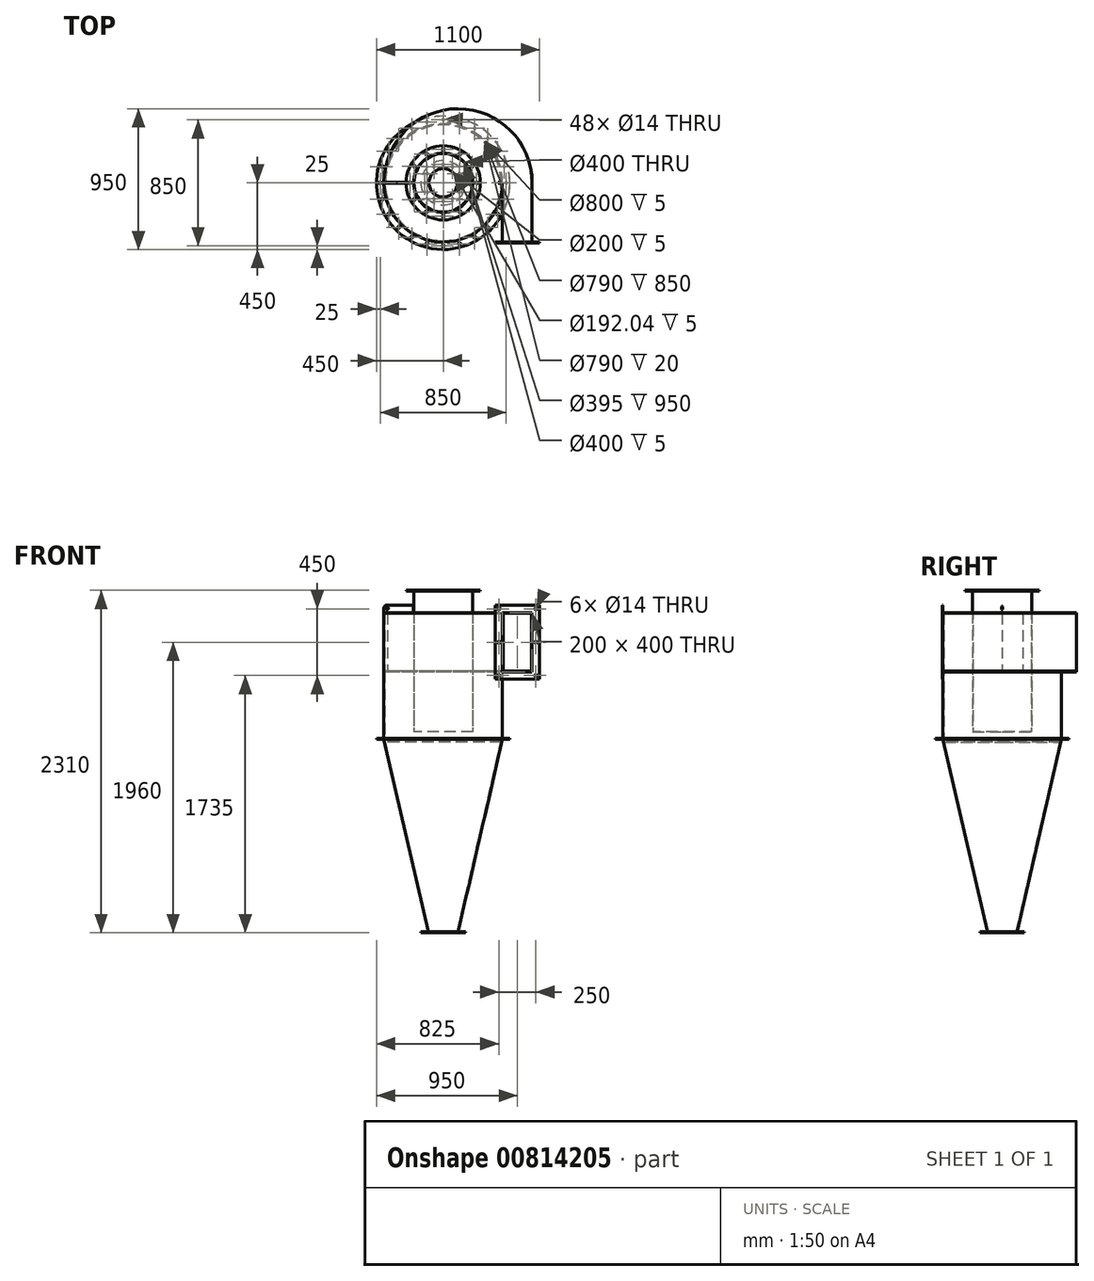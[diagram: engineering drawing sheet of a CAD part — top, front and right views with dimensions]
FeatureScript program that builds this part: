
annotation { "Feature Type Name" : "Feature", "Feature Type Description" : "" }
export const myFeature = defineFeature(function(context is Context, id is Id, definition is map)
    precondition{}
    {
        {
            var Q0;
            Q0=qCreatedBy(makeId("Top.planeOp"),FACE);
            var sketch = newSketch(context, id + "F0", { "sketchPlane" : qUnion([Q0])});
            skCircle(sketch, "E0", {"center": v(0, 0) * mm, "radius": 150 * mm});
            skCircle(sketch, "E1", {"center": v(0, 0) * mm, "radius": 100 * mm});
            skLineSegment(sketch, "E2", {"start": v(0, 100) * mm, "end": v(0, 150) * mm, "construction": true});
            skCircle(sketch, "E3", {"center": v(0, 125) * mm, "radius": 7 * mm});
            skCircle(sketch, "E4.1.0", {"center": v(-62.5, 108.25) * mm, "radius": 7 * mm});
            skCircle(sketch, "E4.2.0", {"center": v(-108.25, 62.5) * mm, "radius": 7 * mm});
            skCircle(sketch, "E4.3.0", {"center": v(-125, 0) * mm, "radius": 7 * mm});
            skCircle(sketch, "E4.4.0", {"center": v(-108.25, -62.5) * mm, "radius": 7 * mm});
            skCircle(sketch, "E4.5.0", {"center": v(-62.5, -108.25) * mm, "radius": 7 * mm});
            skCircle(sketch, "E4.6.0", {"center": v(0, -125) * mm, "radius": 7 * mm});
            skCircle(sketch, "E4.7.0", {"center": v(62.5, -108.25) * mm, "radius": 7 * mm});
            skCircle(sketch, "E4.8.0", {"center": v(108.25, -62.5) * mm, "radius": 7 * mm});
            skCircle(sketch, "E4.9.0", {"center": v(125, 0) * mm, "radius": 7 * mm});
            skCircle(sketch, "E4.10.0", {"center": v(108.25, 62.5) * mm, "radius": 7 * mm});
            skCircle(sketch, "E4.11.0", {"center": v(62.5, 108.25) * mm, "radius": 7 * mm});
            skSolve(sketch);
        }
        {
            var Q0;
            Q0=makeQuery(id+"F0.imprint","IMPRINT",FACE,{"disambiguationData":[TD([[makeQuery(id+"F0.imprint","IMPRINT",EDGE,{"derivedFrom":sQuery(id+"F0.wireOp",EDGE,"E0")}),1.0]])]});
            extrude(context, id + "F1", {"entities" : qUnion([Q0]), "oppositeDirection" : true, "depth" : 5 * mm, "offsetDistance" : 25 * mm});
        }
        {
            var Q0;
            Q0=makeQuery(id+"F0.imprint","IMPRINT",FACE,{"disambiguationData":[TD([[makeQuery(id+"F0.imprint","IMPRINT",EDGE,{"derivedFrom":sQuery(id+"F0.wireOp",EDGE,"E0")}),1.0]])]});
            cPlane(context, id + "F2", {"entities" : qUnion([Q0]), "cplaneType" : CPlaneType.OFFSET, "offset" : 1300 * mm, "width" : 150 * mm, "height" : 150 * mm});
        }
        {
            var Q0;
            Q0=qCreatedBy(id+"F2.planeOp",FACE);
            var sketch = newSketch(context, id + "F3", { "sketchPlane" : qUnion([Q0])});
            skCircle(sketch, "E5", {"center": v(0, 0) * mm, "radius": 400 * mm});
            skCircle(sketch, "E6", {"center": v(0, 0) * mm, "radius": 450 * mm});
            skLineSegment(sketch, "E7", {"start": v(0, 400) * mm, "end": v(0, 450) * mm, "construction": true});
            skCircle(sketch, "E8", {"center": v(0, 425) * mm, "radius": 7 * mm});
            skCircle(sketch, "E9.1.0", {"center": v(-110, 410.52) * mm, "radius": 7 * mm});
            skCircle(sketch, "E9.2.0", {"center": v(-212.5, 368.06) * mm, "radius": 7 * mm});
            skCircle(sketch, "E9.3.0", {"center": v(-300.52, 300.52) * mm, "radius": 7 * mm});
            skCircle(sketch, "E9.4.0", {"center": v(-368.06, 212.5) * mm, "radius": 7 * mm});
            skCircle(sketch, "E9.5.0", {"center": v(-410.52, 110) * mm, "radius": 7 * mm});
            skCircle(sketch, "E9.6.0", {"center": v(-425, 0) * mm, "radius": 7 * mm});
            skCircle(sketch, "E9.7.0", {"center": v(-410.52, -110) * mm, "radius": 7 * mm});
            skCircle(sketch, "E9.8.0", {"center": v(-368.06, -212.5) * mm, "radius": 7 * mm});
            skCircle(sketch, "E9.9.0", {"center": v(-300.52, -300.52) * mm, "radius": 7 * mm});
            skCircle(sketch, "E9.10.0", {"center": v(-212.5, -368.06) * mm, "radius": 7 * mm});
            skCircle(sketch, "E9.11.0", {"center": v(-110, -410.52) * mm, "radius": 7 * mm});
            skCircle(sketch, "E9.12.0", {"center": v(0, -425) * mm, "radius": 7 * mm});
            skCircle(sketch, "E9.13.0", {"center": v(110, -410.52) * mm, "radius": 7 * mm});
            skCircle(sketch, "E9.14.0", {"center": v(212.5, -368.06) * mm, "radius": 7 * mm});
            skCircle(sketch, "E9.15.0", {"center": v(300.52, -300.52) * mm, "radius": 7 * mm});
            skCircle(sketch, "E9.16.0", {"center": v(368.06, -212.5) * mm, "radius": 7 * mm});
            skCircle(sketch, "E9.17.0", {"center": v(410.52, -110) * mm, "radius": 7 * mm});
            skCircle(sketch, "E9.18.0", {"center": v(425, 0) * mm, "radius": 7 * mm});
            skCircle(sketch, "E9.19.0", {"center": v(410.52, 110) * mm, "radius": 7 * mm});
            skCircle(sketch, "E9.20.0", {"center": v(368.06, 212.5) * mm, "radius": 7 * mm});
            skCircle(sketch, "E9.21.0", {"center": v(300.52, 300.52) * mm, "radius": 7 * mm});
            skCircle(sketch, "E9.22.0", {"center": v(212.5, 368.06) * mm, "radius": 7 * mm});
            skCircle(sketch, "E9.23.0", {"center": v(110, 410.52) * mm, "radius": 7 * mm});
            skSolve(sketch);
        }
        {
            var Q0;
            Q0=makeQuery(id+"F3.imprint","IMPRINT",FACE,{"disambiguationData":[TD([[makeQuery(id+"F3.imprint","IMPRINT",EDGE,{"derivedFrom":sQuery(id+"F3.wireOp",EDGE,"E5")}),-1.0]])]});
            extrude(context, id + "F4", {"entities" : qUnion([Q0]), "depth" : 5 * mm, "offsetDistance" : 25 * mm});
        }
        {
            var Q0;
            Q0=qCreatedBy(makeId("Top.planeOp"),FACE);
            var sketch = newSketch(context, id + "F5", { "sketchPlane" : qUnion([Q0])});
            skCircle(sketch, "E10", {"center": v(0, 0) * mm, "radius": 100 * mm});
            skSolve(sketch);
        }
        {
            var Q0;
            Q0=qCreatedBy(id+"F2.planeOp",FACE);
            var sketch = newSketch(context, id + "F6", { "sketchPlane" : qUnion([Q0])});
            skCircle(sketch, "E11", {"center": v(0, 0) * mm, "radius": 400 * mm});
            skLineSegment(sketch, "E12", {"start": v(0, 0) * mm, "end": v(0, 559.62) * mm, "construction": true});
            skSolve(sketch);
        }
        {
            var Q0;
            Q0=makeQuery(id+"F5.imprint","IMPRINT",FACE,{"disambiguationData":[TD([[makeQuery(id+"F5.imprint","IMPRINT",EDGE,{"derivedFrom":sQuery(id+"F5.wireOp",EDGE,"E10")}),1.0]])]});
            var Q1;
            Q1=makeQuery(id+"F6.imprint","IMPRINT",FACE,{"disambiguationData":[TD([[makeQuery(id+"F6.imprint","IMPRINT",EDGE,{"derivedFrom":sQuery(id+"F6.wireOp",EDGE,"E11")}),1.0]])]});
            loft(context, id + "F7", {"sheetProfilesArray" : [{ "sheetProfileEntities" : qUnion([Q0]) }, { "sheetProfileEntities" : qUnion([Q1]) }]});
        }
        {
            var Q0;
            Q0=makeQuery(id+"F7.opLoft","CAP_FACE",FACE,{"disambiguationData":[OSD([makeQuery(id+"F6.imprint","IMPRINT",FACE,{"disambiguationData":[TD([[makeQuery(id+"F6.imprint","IMPRINT",EDGE,{"derivedFrom":sQuery(id+"F6.wireOp",EDGE,"E11")}),1.0]])]})])],"isStart":true});
            shell(context, id + "F8", {"entities" : qUnion([Q0]), "thickness" : 5 * mm});
        }
        {
            var Q0;
            Q0=makeQuery(id+"F8.opShell","OFFSET_FACE",FACE,{"disambiguationData":[OSD([makeQuery(id+"F5.imprint","IMPRINT",FACE,{"disambiguationData":[TD([[makeQuery(id+"F5.imprint","IMPRINT",EDGE,{"derivedFrom":sQuery(id+"F5.wireOp",EDGE,"E10")}),1.0]])]})])]});
            extrude(context, id + "F9", {"entities" : qUnion([Q0]), "operationType" : NewBodyOperationType.REMOVE, "oppositeDirection" : true, "depth" : 25 * mm, "offsetDistance" : 25 * mm});
        }
        {
            var Q0;
            Q0=qSketchRegion(id+"F6",true);
            extrude(context, id + "F10", {"entities" : qUnion([Q0]), "depth" : 850 * mm, "offsetDistance" : 25 * mm});
        }
        {
            var Q0;
            Q0=makeQuery(id+"F10.opExtrude","CAP_FACE",FACE,{"disambiguationData":[OSD([sQuery(id+"F6.wireOp",EDGE,"E11")])],"isStart":false});
            shell(context, id + "F11", {"entities" : qUnion([Q0]), "thickness" : 5 * mm});
        }
        {
            var Q0;
            {var subQ0=sQuery(id+"F6.wireOp",EDGE,"E11");Q0=makeQuery(id+"F11.opShell","OFFSET_FACE",FACE,{"disambiguationData":[OSD([subQ0]),TDD([makeQuery(id+"F10.opExtrude","CAP_FACE",FACE,{"disambiguationData":[OSD([subQ0])],"isStart":true})])]});}
            extrude(context, id + "F12", {"entities" : qUnion([Q0]), "operationType" : NewBodyOperationType.REMOVE, "oppositeDirection" : true, "depth" : 25 * mm, "offsetDistance" : 25 * mm});
        }
        {
            var Q0;
            Q0=makeQuery(id+"F4.opExtrude","CAP_FACE",FACE,{"disambiguationData":[OSD([sQuery(id+"F3.wireOp",EDGE,"E5"),sQuery(id+"F3.wireOp",EDGE,"E6"),sQuery(id+"F3.wireOp",EDGE,"E8"),sQuery(id+"F3.wireOp",EDGE,"E9.1.0"),sQuery(id+"F3.wireOp",EDGE,"E9.2.0"),sQuery(id+"F3.wireOp",EDGE,"E9.3.0"),sQuery(id+"F3.wireOp",EDGE,"E9.4.0"),sQuery(id+"F3.wireOp",EDGE,"E9.5.0"),sQuery(id+"F3.wireOp",EDGE,"E9.6.0"),sQuery(id+"F3.wireOp",EDGE,"E9.7.0"),sQuery(id+"F3.wireOp",EDGE,"E9.8.0"),sQuery(id+"F3.wireOp",EDGE,"E9.9.0"),sQuery(id+"F3.wireOp",EDGE,"E9.10.0"),sQuery(id+"F3.wireOp",EDGE,"E9.11.0"),sQuery(id+"F3.wireOp",EDGE,"E9.12.0"),sQuery(id+"F3.wireOp",EDGE,"E9.13.0"),sQuery(id+"F3.wireOp",EDGE,"E9.14.0"),sQuery(id+"F3.wireOp",EDGE,"E9.15.0"),sQuery(id+"F3.wireOp",EDGE,"E9.16.0"),sQuery(id+"F3.wireOp",EDGE,"E9.17.0"),sQuery(id+"F3.wireOp",EDGE,"E9.18.0"),sQuery(id+"F3.wireOp",EDGE,"E9.19.0"),sQuery(id+"F3.wireOp",EDGE,"E9.20.0"),sQuery(id+"F3.wireOp",EDGE,"E9.21.0"),sQuery(id+"F3.wireOp",EDGE,"E9.22.0"),sQuery(id+"F3.wireOp",EDGE,"E9.23.0")])],"isStart":false});
            cPlane(context, id + "F13", {"entities" : qUnion([Q0]), "cplaneType" : CPlaneType.OFFSET, "offset" : 450 * mm, "width" : 150 * mm, "height" : 150 * mm});
        }
        {
            var Q0;
            Q0=qCreatedBy(id+"F13.planeOp",FACE);
            var sketch = newSketch(context, id + "F14", { "sketchPlane" : qUnion([Q0])});
            skLineSegment(sketch, "E13.bottom", {"start": v(-526.39, 0) * mm, "end": v(526.39, 0) * mm});
            skLineSegment(sketch, "E13.top", {"start": v(-526.39, 503.66) * mm, "end": v(526.39, 503.66) * mm});
            skLineSegment(sketch, "E13.left", {"start": v(-526.39, 0) * mm, "end": v(-526.39, 503.66) * mm});
            skLineSegment(sketch, "E13.right", {"start": v(526.39, 0) * mm, "end": v(526.39, 503.66) * mm});
            skSolve(sketch);
        }
        {
            var Q0;
            Q0=makeQuery(id+"F14.imprint","IMPRINT",FACE,{"disambiguationData":[TD([[makeQuery(id+"F14.imprint","IMPRINT",EDGE,{"derivedFrom":sQuery(id+"F14.wireOp",EDGE,"E13.bottom")}),1.0]])]});
            extrude(context, id + "F15", {"entities" : qUnion([Q0]), "operationType" : NewBodyOperationType.REMOVE, "depth" : 400 * mm, "offsetDistance" : 25 * mm});
        }
        {
            var Q0;
            Q0=qCreatedBy(id+"F13.planeOp",FACE);
            var sketch = newSketch(context, id + "F16", { "sketchPlane" : qUnion([Q0])});
            skArc(sketch, "E14", {"start": v(600, 0) * mm, "mid": v(100, 500) * mm, "end": v(-400, 0) * mm});
            skLineSegment(sketch, "E15", {"start": v(-400, 0) * mm, "end": v(721.85, 0) * mm, "construction": true});
            skLineSegment(sketch, "E16", {"start": v(600, 0) * mm, "end": v(600, -400) * mm});
            skLineSegment(sketch, "E17", {"start": v(600, -400) * mm, "end": v(400, -400) * mm});
            skLineSegment(sketch, "E18", {"start": v(400, -400) * mm, "end": v(400, 0) * mm});
            skArc(sketch, "E19", {"start": v(400, 0) * mm, "mid": v(0, 400) * mm, "end": v(-400, 0) * mm});
            skSolve(sketch);
        }
        {
            var Q0;
            Q0=makeQuery(id+"F16.imprint","IMPRINT",FACE,{"disambiguationData":[TD([[makeQuery(id+"F16.imprint","IMPRINT",EDGE,{"derivedFrom":sQuery(id+"F16.wireOp",EDGE,"E14")}),1.0]])]});
            extrude(context, id + "F17", {"entities" : qUnion([Q0]), "depth" : 5 * mm, "offsetDistance" : 25 * mm});
        }
        {
            var Q0;
            Q0=makeQuery(id+"F17.opExtrude","CAP_FACE",FACE,{"disambiguationData":[OSD([sQuery(id+"F16.wireOp",EDGE,"E14"),sQuery(id+"F16.wireOp",EDGE,"E16"),sQuery(id+"F16.wireOp",EDGE,"E17"),sQuery(id+"F16.wireOp",EDGE,"E18"),sQuery(id+"F16.wireOp",EDGE,"E19")])],"isStart":false});
            var sketch = newSketch(context, id + "F18", { "sketchPlane" : qUnion([Q0])});
            skLineSegment(sketch, "E20.bottom", {"start": v(400, -400) * mm, "end": v(405, -400) * mm});
            skLineSegment(sketch, "E20.top", {"start": v(400, 0) * mm, "end": v(405, 0) * mm});
            skLineSegment(sketch, "E20.left", {"start": v(400, -400) * mm, "end": v(400, 0) * mm});
            skLineSegment(sketch, "E20.right", {"start": v(405, -400) * mm, "end": v(405, 0) * mm});
            skSolve(sketch);
        }
        {
            var Q0;
            Q0=makeQuery(id+"F18.imprint","IMPRINT",FACE,{"disambiguationData":[TD([[makeQuery(id+"F18.imprint","IMPRINT",EDGE,{"derivedFrom":sQuery(id+"F18.wireOp",EDGE,"E20.bottom")}),-1.0]])]});
            extrude(context, id + "F19", {"entities" : qUnion([Q0]), "operationType" : NewBodyOperationType.ADD, "depth" : 390 * mm, "offsetDistance" : 25 * mm});
        }
        {
            var Q0;
            Q0=qCreatedBy(id+"F13.planeOp",FACE);
            cPlane(context, id + "F20", {"entities" : qUnion([Q0]), "cplaneType" : CPlaneType.OFFSET, "offset" : 395 * mm, "width" : 150 * mm, "height" : 150 * mm});
        }
        {
            var Q0;
            Q0=qCreatedBy(id+"F20.planeOp",FACE);
            var sketch = newSketch(context, id + "F21", { "sketchPlane" : qUnion([Q0])});
            skArc(sketch, "E21", {"start": v(600, 0) * mm, "mid": v(100, 500) * mm, "end": v(-400, 0) * mm});
            skLineSegment(sketch, "E22", {"start": v(-400, 0) * mm, "end": v(721.85, 0) * mm, "construction": true});
            skLineSegment(sketch, "E23", {"start": v(600, 0) * mm, "end": v(600, -400) * mm});
            skLineSegment(sketch, "E24", {"start": v(600, -400) * mm, "end": v(400, -400) * mm});
            skLineSegment(sketch, "E25", {"start": v(400, -400) * mm, "end": v(400, 0) * mm});
            skArc(sketch, "E26", {"start": v(-400, 0) * mm, "mid": v(0, -400) * mm, "end": v(400, 0) * mm});
            skCircle(sketch, "E27", {"center": v(0, 0) * mm, "radius": 200 * mm});
            skSolve(sketch);
        }
        {
            var Q0;
            Q0=makeQuery(id+"F21.imprint","IMPRINT",FACE,{"disambiguationData":[TD([[makeQuery(id+"F21.imprint","IMPRINT",EDGE,{"derivedFrom":sQuery(id+"F21.wireOp",EDGE,"E21")}),1.0]])]});
            extrude(context, id + "F22", {"entities" : qUnion([Q0]), "depth" : 5 * mm, "offsetDistance" : 25 * mm});
        }
        {
            var Q0;
            Q0=qCreatedBy(id+"F20.planeOp",FACE);
            var sketch = newSketch(context, id + "F23", { "sketchPlane" : qUnion([Q0])});
            skCircle(sketch, "E28", {"center": v(0, 0) * mm, "radius": 199.5 * mm});
            skCircle(sketch, "E29.0", {"center": v(0, 0) * mm, "radius": 197.5 * mm});
            skSolve(sketch);
        }
        {
            var Q0;
            Q0=makeQuery(id+"F23.imprint","IMPRINT",FACE,{"disambiguationData":[TD([[makeQuery(id+"F23.imprint","IMPRINT",EDGE,{"derivedFrom":sQuery(id+"F23.wireOp",EDGE,"E28")}),1.0]])]});
            extrude(context, id + "F24", {"entities" : qUnion([Q0]), "depth" : 950 * mm, "offsetDistance" : 25 * mm});
        }
        {
            var Q0;
            Q0=qCreatedBy(makeId("Front.planeOp"),FACE);
            var sketch = newSketch(context, id + "F25", { "sketchPlane" : qUnion([Q0])});
            skLineSegment(sketch, "E30", {"start": v(0, 0) * mm, "end": v(0, 3754) * mm, "construction": true});
            skSolve(sketch);
        }
        {
            var Q0;
            Q0=makeQuery(id+"F24.opExtrude","SWEPT_BODY",BODY,{"disambiguationData":[OSD([sQuery(id+"F23.wireOp",EDGE,"E28"),sQuery(id+"F23.wireOp",EDGE,"E29.0")])]});
            var Q1;
            Q1=sQuery(id+"F25.wireOp",EDGE,"E30");
            var Q2;
            Q2=sQuery(id+"F25.wireOp",EDGE,"E30");
            transform(context, id + "F26", {"entities" : qUnion([Q0]), "transformType" : TransformType.TRANSLATION_DISTANCE, "transformDirection" : qUnion([Q2]), "distance" : 800 * mm, "oppositeDirection" : true, "makeCopy" : false});
        }
        {
            var Q0;
            Q0=makeQuery(id+"F22.opExtrude","SWEPT_FACE",FACE,{"disambiguationData":[OSD([sQuery(id+"F21.wireOp",EDGE,"E24")])]});
            var sketch = newSketch(context, id + "F27", { "sketchPlane" : qUnion([Q0])});
            skLineSegment(sketch, "E31.bottom", {"start": v(400, 2155) * mm, "end": v(600, 2155) * mm});
            skLineSegment(sketch, "E31.top", {"start": v(400, 1755) * mm, "end": v(600, 1755) * mm});
            skLineSegment(sketch, "E31.left", {"start": v(400, 2155) * mm, "end": v(400, 1755) * mm});
            skLineSegment(sketch, "E31.right", {"start": v(600, 2155) * mm, "end": v(600, 1755) * mm});
            skLineSegment(sketch, "E32.0", {"start": v(650, 2205) * mm, "end": v(650, 1705) * mm});
            skLineSegment(sketch, "E32.1", {"start": v(350, 2205) * mm, "end": v(650, 2205) * mm});
            skLineSegment(sketch, "E32.2", {"start": v(350, 2205) * mm, "end": v(350, 1705) * mm});
            skLineSegment(sketch, "E32.3", {"start": v(350, 1705) * mm, "end": v(650, 1705) * mm});
            skLineSegment(sketch, "E33.0", {"start": v(375, 2180) * mm, "end": v(375, 1730) * mm, "construction": true});
            skLineSegment(sketch, "E33.1", {"start": v(375, 2180) * mm, "end": v(625, 2180) * mm, "construction": true});
            skLineSegment(sketch, "E33.2", {"start": v(625, 2180) * mm, "end": v(625, 1730) * mm, "construction": true});
            skLineSegment(sketch, "E33.3", {"start": v(375, 1730) * mm, "end": v(625, 1730) * mm});
            skCircle(sketch, "E34", {"center": v(375, 2180) * mm, "radius": 7 * mm});
            skCircle(sketch, "E35", {"center": v(625, 2180) * mm, "radius": 7 * mm});
            skCircle(sketch, "E36", {"center": v(625, 1730) * mm, "radius": 7 * mm});
            skCircle(sketch, "E37", {"center": v(375, 1730) * mm, "radius": 7 * mm});
            skCircle(sketch, "E38", {"center": v(375, 1955) * mm, "radius": 7 * mm});
            skCircle(sketch, "E39", {"center": v(625, 1955) * mm, "radius": 7 * mm});
            skSolve(sketch);
        }
        {
            var Q0;
            {var subQ3=sQuery(id+"F27.wireOp",EDGE,"E31.bottom");Q0=makeQuery(id+"F27.imprint","IMPRINT",FACE,{"disambiguationData":[TD([[makeQuery(id+"F27.imprint","IMPRINT",EDGE,{"derivedFrom":subQ3}),-1.0]])]});}
            extrude(context, id + "F28", {"entities" : qUnion([Q0]), "depth" : 5 * mm, "offsetDistance" : 25 * mm});
        }
        {
            var Q0;
            Q0=qCreatedBy(makeId("Front.planeOp"),FACE);
            var sketch = newSketch(context, id + "F29", { "sketchPlane" : qUnion([Q0])});
            skLineSegment(sketch, "E40.bottom", {"start": v(-200.23, 2155) * mm, "end": v(-400.23, 2155) * mm});
            skLineSegment(sketch, "E40.top", {"start": v(-200.23, 2205) * mm, "end": v(-380.23, 2205) * mm});
            skLineSegment(sketch, "E40.left", {"start": v(-200.23, 2155) * mm, "end": v(-200.23, 2205) * mm});
            skLineSegment(sketch, "E40.right", {"start": v(-400.23, 2155) * mm, "end": v(-400.23, 2185) * mm});
            skPoint(sketch, "E41.visualSharp", {"position": v(-400.23, 2205) * mm});
            skArc(sketch, "E41.filletArc", {"start": v(-380.23, 2205) * mm, "mid": v(-394.37, 2199.14) * mm, "end": v(-400.23, 2185) * mm});
            skCircle(sketch, "E42", {"center": v(-380.23, 2185) * mm, "radius": 10 * mm});
            skCircle(sketch, "E43.MirrorC", {"center": v(380.23, 2185) * mm, "radius": 10 * mm});
            skArc(sketch, "E44.MirrorCS", {"start": v(380.23, 2205) * mm, "mid": v(394.37, 2199.14) * mm, "end": v(400.23, 2185) * mm});
            skPoint(sketch, "E45.MirrorP", {"position": v(400.23, 2205) * mm});
            skLineSegment(sketch, "E46.MirrorCS", {"start": v(400.23, 2155) * mm, "end": v(400.23, 2185) * mm});
            skLineSegment(sketch, "E47.MirrorCS", {"start": v(200.23, 2155) * mm, "end": v(200.23, 2205) * mm});
            skLineSegment(sketch, "E48.MirrorCS", {"start": v(200.23, 2155) * mm, "end": v(400.23, 2155) * mm});
            skLineSegment(sketch, "E49.MirrorCS", {"start": v(200.23, 2205) * mm, "end": v(380.23, 2205) * mm});
            skSolve(sketch);
        }
        {
            var Q0;
            Q0=makeQuery(id+"F29.imprint","IMPRINT",FACE,{"disambiguationData":[TD([[makeQuery(id+"F29.imprint","IMPRINT",EDGE,{"derivedFrom":sQuery(id+"F29.wireOp",EDGE,"E40.bottom")}),-1.0]])]});
            var Q1;
            Q1=makeQuery(id+"F29.imprint","IMPRINT",FACE,{"disambiguationData":[TD([[makeQuery(id+"F29.imprint","IMPRINT",EDGE,{"derivedFrom":sQuery(id+"F29.wireOp",EDGE,"E43.MirrorC")}),1.0]])]});
            extrude(context, id + "F30", {"entities" : qUnion([Q0, Q1]), "operationType" : NewBodyOperationType.ADD, "endBound" : BoundingType.SYMMETRIC, "depth" : 5 * mm, "offsetDistance" : 25 * mm});
        }
        {
            var Q0;
            Q0=makeQuery(id+"F24.opExtrude","CAP_FACE",FACE,{"disambiguationData":[OSD([sQuery(id+"F23.wireOp",EDGE,"E28"),sQuery(id+"F23.wireOp",EDGE,"E29.0")])],"isStart":false});
            var sketch = newSketch(context, id + "F31", { "sketchPlane" : qUnion([Q0])});
            skCircle(sketch, "E50", {"center": v(0, 0) * mm, "radius": 200 * mm});
            skCircle(sketch, "E51.0", {"center": v(0, 0) * mm, "radius": 250 * mm});
            skLineSegment(sketch, "E52", {"start": v(0, 200) * mm, "end": v(0, 250) * mm, "construction": true});
            skCircle(sketch, "E53", {"center": v(0, 225) * mm, "radius": 7 * mm});
            skCircle(sketch, "E54.1.0", {"center": v(-112.5, 194.86) * mm, "radius": 7 * mm});
            skCircle(sketch, "E54.2.0", {"center": v(-194.86, 112.5) * mm, "radius": 7 * mm});
            skCircle(sketch, "E54.3.0", {"center": v(-225, 0) * mm, "radius": 7 * mm});
            skCircle(sketch, "E54.4.0", {"center": v(-194.86, -112.5) * mm, "radius": 7 * mm});
            skCircle(sketch, "E54.5.0", {"center": v(-112.5, -194.86) * mm, "radius": 7 * mm});
            skCircle(sketch, "E54.6.0", {"center": v(0, -225) * mm, "radius": 7 * mm});
            skCircle(sketch, "E54.7.0", {"center": v(112.5, -194.86) * mm, "radius": 7 * mm});
            skCircle(sketch, "E54.8.0", {"center": v(194.86, -112.5) * mm, "radius": 7 * mm});
            skCircle(sketch, "E54.9.0", {"center": v(225, 0) * mm, "radius": 7 * mm});
            skCircle(sketch, "E54.10.0", {"center": v(194.86, 112.5) * mm, "radius": 7 * mm});
            skCircle(sketch, "E54.11.0", {"center": v(112.5, 194.86) * mm, "radius": 7 * mm});
            skSolve(sketch);
        }
        {
            var Q0;
            Q0=makeQuery(id+"F31.imprint","IMPRINT",FACE,{"disambiguationData":[TD([[makeQuery(id+"F31.imprint","IMPRINT",EDGE,{"derivedFrom":sQuery(id+"F31.wireOp",EDGE,"E50")}),-1.0]])]});
            extrude(context, id + "F32", {"entities" : qUnion([Q0]), "depth" : 5 * mm, "offsetDistance" : 25 * mm});
        }
        {
            var Q0;
            Q0=makeQuery(id+"F17.opExtrude","CAP_FACE",FACE,{"disambiguationData":[OSD([sQuery(id+"F16.wireOp",EDGE,"E14"),sQuery(id+"F16.wireOp",EDGE,"E16"),sQuery(id+"F16.wireOp",EDGE,"E17"),sQuery(id+"F16.wireOp",EDGE,"E18"),sQuery(id+"F16.wireOp",EDGE,"E19")])],"isStart":false});
            var sketch = newSketch(context, id + "F33", { "sketchPlane" : qUnion([Q0])});
            skArc(sketch, "E55", {"start": v(600, 0) * mm, "mid": v(100, 500) * mm, "end": v(-400, 0) * mm});
            skArc(sketch, "E56.0", {"start": v(595, 0) * mm, "mid": v(100, 495) * mm, "end": v(-395, 0) * mm});
            skLineSegment(sketch, "E57", {"start": v(-400, 0) * mm, "end": v(-395, 0) * mm});
            skLineSegment(sketch, "E58", {"start": v(600, 0) * mm, "end": v(600, -400) * mm});
            skLineSegment(sketch, "E59", {"start": v(600, -400) * mm, "end": v(595, -400) * mm});
            skLineSegment(sketch, "E60", {"start": v(595, -400) * mm, "end": v(595, 0) * mm});
            skSolve(sketch);
        }
        {
            var Q0;
            {var subQ4=sQuery(id+"F33.wireOp",EDGE,"E55");Q0=makeQuery(id+"F33.imprint","IMPRINT",FACE,{"disambiguationData":[TD([[makeQuery(id+"F33.imprint","IMPRINT",EDGE,{"derivedFrom":subQ4}),1.0]])]});}
            extrude(context, id + "F34", {"entities" : qUnion([Q0]), "depth" : 390 * mm, "offsetDistance" : 25 * mm});
        }
    });
